# Revit family: BIMLIB_УголОтливаВнутренний_GRANDLINE
name_source: partatom
category: Обобщенные модели
revit_build: Autodesk Revit 2017 (Build: 20170118_1100(x64)
units: mm (PartAtom-declared; Revit-internal decimal feet)

## family parameters
Всегда вертикально = Нет
Может служить основой для арматурных стержней = Нет
На основе рабочей плоскости = Да
Общий = Нет
При загрузке вырезать с полостями = Нет
Размер круглого соединителя = Использовать диаметр
Тип детали = Нормальный
Точка расчета площади = Нет

## types (5) — shared parameters
ADSK_URL документации изделия = https://www.grandline.ru
ADSK_URL страницы изделия = https://www.grandline.ru
ADSK_Версия Revit = 2017
ADSK_Группирование = Доборные элементы
ADSK_Единица измерения = шт
ADSK_Завод-изготовитель = Grand Line
ADSK_Материал = GL_Drap_RAL7016
ADSK_Обозначение = ГОСТ 19904-90, ГОСТ 14918-80
BL_BIM library = https://bimlib.pro
URL = https://www.grandline.ru
Изготовитель = Grand Line
zero-valued in all types: ADSK_Масса, ADSK_Материал тип подсчета, Отметка по умолчанию

## per-type parameters (varying)
| type | ADSK_Наименование | ADSK_Размер_Глубина | Описание | Поворот_Длина |
| 50мм | Угол отлива внутренний 50 | 50 мм | Угол отлива внутренний 50 | 100 мм |
| 100мм | Угол отлива внутренний 100 | 100 мм | Угол отлива внутренний 100 | 150 мм |
| 150мм | Угол отлива внутренний 150 | 150 мм | Угол отлива внутренний 150 | 200 мм |
| 200мм | Угол отлива внутренний 200 | 200 мм | Угол отлива внутренний 200 | 250 мм |
| 250мм | Угол отлива внутренний 250 | 250 мм | Угол отлива внутренний 250 | 300 мм |
